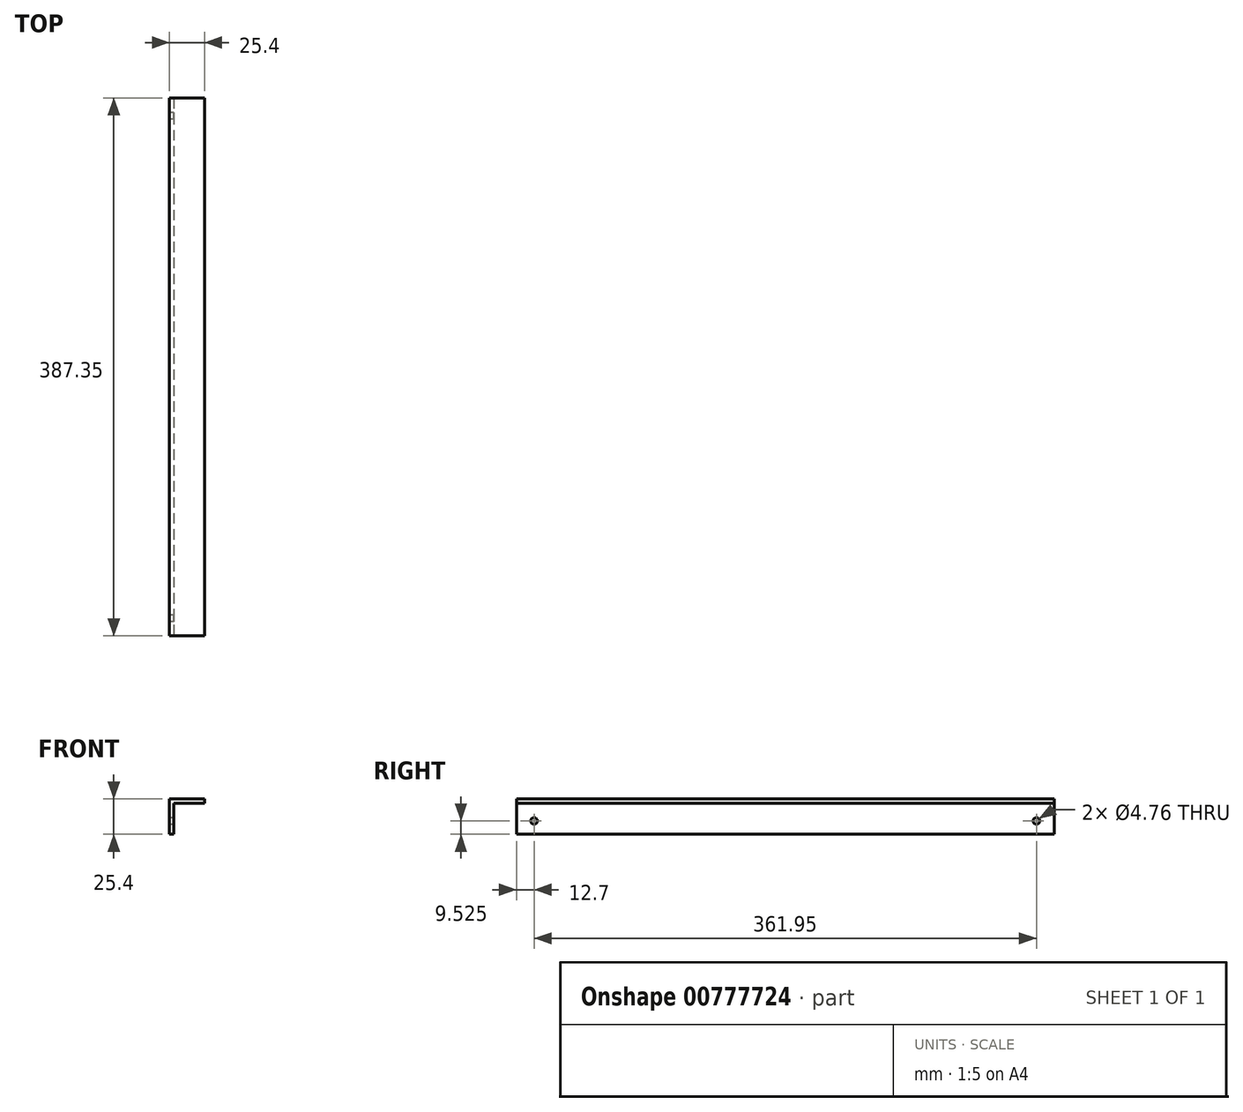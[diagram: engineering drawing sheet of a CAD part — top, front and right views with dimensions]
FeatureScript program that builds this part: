
annotation { "Feature Type Name" : "Feature", "Feature Type Description" : "" }
export const myFeature = defineFeature(function(context is Context, id is Id, definition is map)
    precondition{}
    {
        {
            var Q0;
            Q0=qCreatedBy(makeId("Front.planeOp"),FACE);
            var sketch = newSketch(context, id + "F0", { "sketchPlane" : qUnion([Q0])});
            skLineSegment(sketch, "E0.bottom", {"start": v(0, 0) * mm, "end": v(3.18, 0) * mm});
            skLineSegment(sketch, "E0.top", {"start": v(0, 25.4) * mm, "end": v(25.4, 25.4) * mm});
            skLineSegment(sketch, "E0.left", {"start": v(0, 0) * mm, "end": v(0, 25.4) * mm});
            skLineSegment(sketch, "E0.right", {"start": v(25.4, 22.22) * mm, "end": v(25.4, 25.4) * mm});
            skLineSegment(sketch, "E1.0", {"start": v(3.17, 22.22) * mm, "end": v(25.4, 22.22) * mm});
            skLineSegment(sketch, "E1.1", {"start": v(3.18, 0) * mm, "end": v(3.17, 22.23) * mm});
            skSolve(sketch);
        }
        {
            var Q0;
            Q0 = qSketchRegion(id + "F0", true);
            extrude(context, id + "F1", {"entities" : qUnion([Q0]), "oppositeDirection" : true, "depth" : 387.35 * mm, "offsetDistance" : 25.4 * mm});
        }
        {
            var Q0;
            Q0=makeQuery(id+"F1.opExtrude","SWEPT_FACE",FACE,{"disambiguationData":[OSD([sQuery(id+"F0.wireOp",EDGE,"E0.left")])]});
            var sketch = newSketch(context, id + "F2", { "sketchPlane" : qUnion([Q0])});
            skCircle(sketch, "E2", {"center": v(-12.7, 9.53) * mm, "radius": 2.38 * mm});
            skCircle(sketch, "E3.1.0.0", {"center": v(-374.65, 9.53) * mm, "radius": 2.38 * mm});
            skLineSegment(sketch, "E3.direction1", {"start": v(-12.7, 9.53) * mm, "end": v(-374.65, 9.53) * mm, "construction": true});
            skSolve(sketch);
        }
        {
            var Q0;
            Q0 = qSketchRegion(id + "F2", true);
            extrude(context, id + "F3", {"entities" : qUnion([Q0]), "operationType" : NewBodyOperationType.REMOVE, "oppositeDirection" : true, "depth" : 3.17 * mm, "offsetDistance" : 25.4 * mm});
        }
    });
